# Revit family: Urinal-Wall_Mount-KOHLER-STRUKTURA-K-5889T_1
name_source: partatom
category: Plumbing Fixtures
revit_build: Autodesk Revit 2017 (Build: 20160225_1515(x64)
units: mm (PartAtom-declared; Revit-internal decimal feet)

## family parameters
Cut with Voids When Loaded = No
Host = Face
OmniClass Number = 23.31.21.00
OmniClass Title = Urinals
Part Type = Normal
Room Calculation Point = No
Round Connector Dimension = Use Diameter
Shared = No

## types (2) — shared parameters
ADA Compliant = No
Assembly Code = D2010200
CW Connection = Yes
Cold Water Inlet = Cold Water Inlet
Date Modified = 03/24/2021
Default Elevation = 0"
Finish = Kohler-Vitreous_China-0-White
Flow Rate = 0 GPM
Flush Rate- GPF = GPF
Flush Rate- LPF = LPF
HW Connection = No
Height = 37 1/2"
Hot Water Inlet = Hot Water Inlet
Length = 15 11/16"
Manufacturer = KOHLER Co.
Master Format 2014 = 22 41 13.16
Master Format 2014 Name = Residential Urinals
Material = Vitreous China
Pressure = 0.00 psi
Product Documentation Link = https://files.kohler.com.cn
Product Name = STRUKTURA
Rough In = 4 3/4"
URL = http://www.kohler.com.cn
Vent Connection = No
Waste Connection = Yes
Waste Water Outlet = Waste Water Outlet
WaterSense Certified = No
Width = 14 9/16"

## per-type parameters (varying)
| type | A | Connector Angle | Connector Dist | Coonector Diameter | Description | Model | Rear Inlet Connection | Top Inlet Connection | Type |
| Rear Inlet Connection, 0- White | 3 5/8" | 90.00° | 2 9/16" | 1/2" | STRUKTURA FLOOR STANDING URINAL (REAR) | K-5889T-ER-0 | Yes | No | 1 |
| Top Inlet Connection, 0- White | 0" | 0.00° | 0" | 3/4" | STRUKTURA FLOOR STANDING URINAL (TOP) | K-5889T-ET-0 | No | Yes | 2 |

## geometry (parser evidence)
native form markers: Sweep x5
no freeform markers — native parametric forms only
